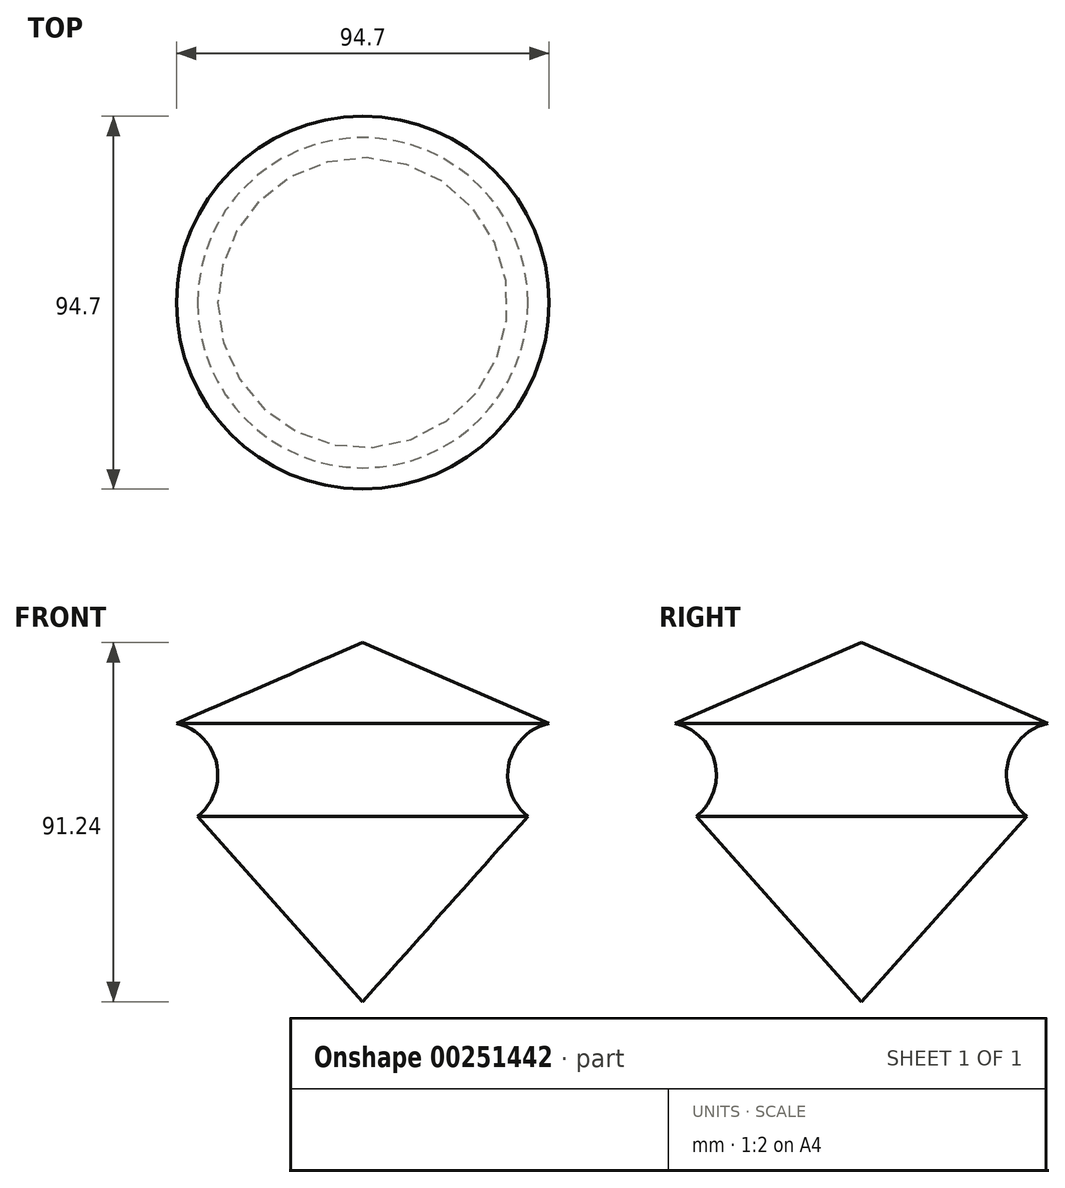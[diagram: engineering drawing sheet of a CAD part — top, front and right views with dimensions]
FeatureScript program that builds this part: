
annotation { "Feature Type Name" : "Feature", "Feature Type Description" : "" }
export const myFeature = defineFeature(function(context is Context, id is Id, definition is map)
    precondition{}
    {
        {
            var Q0;
            Q0=qCreatedBy(makeId("Front.planeOp"),FACE);
            var sketch = newSketch(context, id + "F0", { "sketchPlane" : qUnion([Q0])});
            skLineSegment(sketch, "E0", {"start": v(0, 0) * mm, "end": v(0, 91.24) * mm});
            skLineSegment(sketch, "E1", {"start": v(0, 91.24) * mm, "end": v(47.35, 70.7) * mm});
            skArc(sketch, "E2", {"start": v(47.35, 70.7) * mm, "mid": v(37.16, 60.6) * mm, "end": v(41.97, 47.09) * mm});
            skLineSegment(sketch, "E3", {"start": v(41.97, 47.09) * mm, "end": v(0, 0) * mm});
            skSolve(sketch);
        }
        {
            var Q0;
            Q0 = qSketchRegion(id + "F0", true);
            var Q1;
            Q1=sQuery(id+"F0.wireOp",EDGE,"E0");
            revolve(context, id + "F1", {"entities" : qUnion([Q0]), "axis" : qUnion([Q1]), "revolveType" : RevolveType.FULL});
        }
    });
